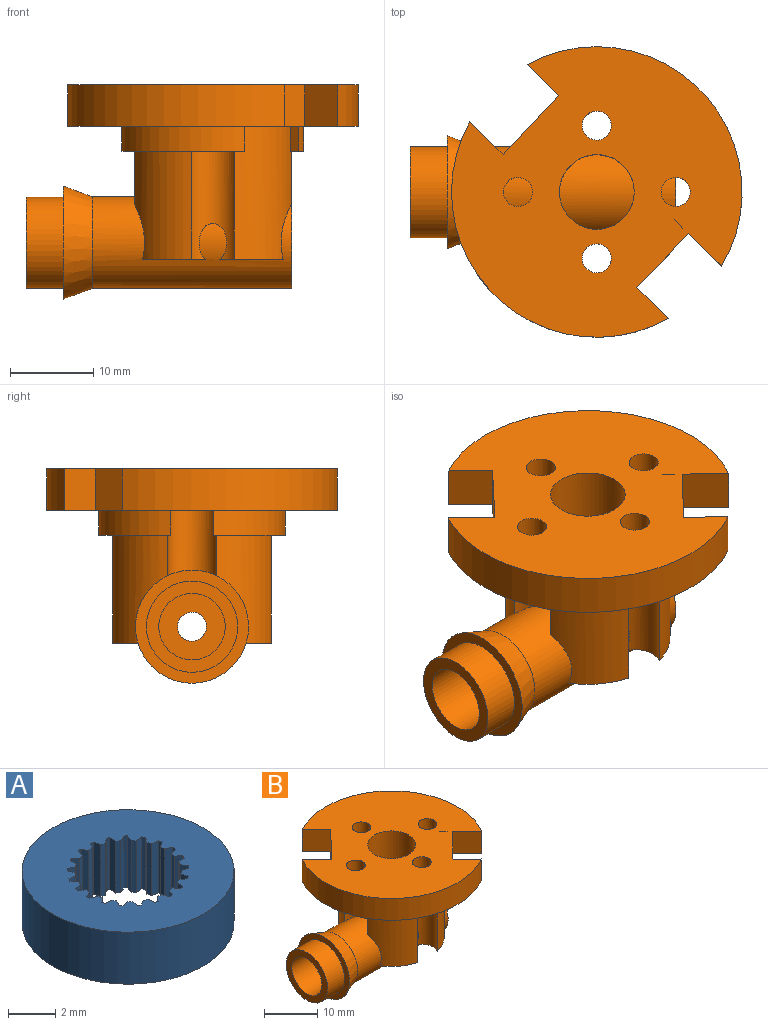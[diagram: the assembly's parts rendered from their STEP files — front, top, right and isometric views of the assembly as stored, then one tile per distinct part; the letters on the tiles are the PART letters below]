
ASSEMBLY  parts=2 mates=1
PART A: 87 faces, bbox 9x9x2.7 mm
  f0: cylinder r=2.58mm len=2.7mm, axis (0,0,-1), area 0.5mm2, adj f22,f24,f25,f57
  f1: cylinder r=2.58mm len=2.7mm, axis (0,0,-1), area 0.5mm2, adj f24,f25,f55,f56
  f2: cylinder r=2.58mm len=2.7mm, axis (0,0,-1), area 0.5mm2, adj f24,f25,f53,f54
  f3: cylinder r=2.58mm len=2.7mm, axis (0,0,-1), area 0.5mm2, adj f24,f25,f51,f52
  f4: cylinder r=2.58mm len=2.7mm, axis (0,0,-1), area 0.5mm2, adj f24,f25,f49,f50
  f5: cylinder r=2.58mm len=2.7mm, axis (0,0,-1), area 0.5mm2, adj f24,f25,f47,f48
  f6: cylinder r=2.58mm len=2.7mm, axis (0,0,-1), area 0.5mm2, adj f24,f25,f45,f46
  f7: cylinder r=2.58mm len=2.7mm, axis (0,0,-1), area 0.5mm2, adj f24,f25,f43,f44
  f8: cylinder r=2.58mm len=2.7mm, axis (0,0,-1), area 0.5mm2, adj f24,f25,f41,f42
  f9: cylinder r=2.58mm len=2.7mm, axis (0,0,-1), area 0.5mm2, adj f24,f25,f39,f40
  f10: cylinder r=2.58mm len=2.7mm, axis (0,0,-1), area 0.5mm2, adj f24,f25,f37,f38
  f11: cylinder r=2.58mm len=2.7mm, axis (0,0,-1), area 0.5mm2, adj f24,f25,f35,f36
  f12: cylinder r=2.58mm len=2.7mm, axis (0,0,-1), area 0.5mm2, adj f24,f25,f33,f34
  f13: cylinder r=2.58mm len=2.7mm, axis (0,0,-1), area 0.5mm2, adj f24,f25,f31,f32
  f14: cylinder r=2.58mm len=2.7mm, axis (0,0,-1), area 0.5mm2, adj f24,f25,f29,f30
  f15: cylinder r=2.58mm len=2.7mm, axis (0,0,-1), area 0.5mm2, adj f24,f25,f27,f28
  f16: cylinder r=2.58mm len=2.7mm, axis (0,0,-1), area 0.5mm2, adj f24,f25,f26,f64
  f17: cylinder r=2.58mm len=2.7mm, axis (0,0,-1), area 0.5mm2, adj f24,f25,f63,f65
  f18: cylinder r=2.58mm len=2.7mm, axis (0,0,-1), area 0.5mm2, adj f24,f25,f61,f62
  f19: cylinder r=2.58mm len=2.7mm, axis (0,0,-1), area 0.5mm2, adj f24,f25,f58,f60
  f20: plane 2.7x0.31mm, normal (0.86,-0.51,0), area 1mm2, adj f21,f24,f25,f86
  f21: cylinder r=2.58mm len=2.7mm, axis (0,0,-1), area 0.5mm2, adj f20,f24,f25,f59
  f22: plane 2.7x0.31mm, normal (-0.86,-0.51,0), area 1mm2, adj f0,f24,f25,f86
  f23: cylinder r=4.5mm len=9mm, axis (0,0,-1), area 76.3mm2, adj f24,f25
  f24: plane 9x9mm, normal (0,0,1), area 45.6mm2, adj f0,f1,f2,f3,f4,f5,f6,f7
  f25: plane 9x9mm, normal (0,0,-1), area 45.6mm2, adj f0,f1,f2,f3,f4,f5,f6,f7
  f26: plane 2.7x0.3mm, normal (-0.58,0.82,0), area 1mm2, adj f16,f24,f25,f85
  f27: plane 2.7x0.32mm, normal (-0.45,-0.89,0), area 1mm2, adj f15,f24,f25,f85
  f28: plane 2.7x0.34mm, normal (-0.31,0.95,0), area 1mm2, adj f15,f24,f25,f84
  f29: plane 2.7x0.26mm, normal (-0.69,-0.72,0), area 1mm2, adj f14,f24,f25,f84
  f30: plane 2.7x0.36mm, normal (-0.02,1,0), area 1mm2, adj f14,f24,f25,f83
  f31: plane 2.7x0.32mm, normal (-0.87,-0.49,0), area 1mm2, adj f13,f24,f25,f83
  f32: plane 2.7x0.35mm, normal (0.28,0.96,0), area 1mm2, adj f13,f24,f25,f82
  f33: plane 2.7x0.35mm, normal (-0.98,-0.21,0), area 1mm2, adj f12,f24,f25,f82
  f34: plane 2.7x0.3mm, normal (0.55,0.84,0), area 1mm2, adj f12,f24,f25,f81
  f35: plane 2.7x0.36mm, normal (-1,0.09,0), area 1mm2, adj f11,f24,f25,f81
  f36: plane 2.7x0.28mm, normal (0.77,0.64,0), area 1mm2, adj f11,f24,f25,f80
  f37: plane 2.7x0.33mm, normal (-0.92,0.38,0), area 1mm2, adj f10,f24,f25,f80
  f38: plane 2.7x0.33mm, normal (0.92,0.38,0), area 1mm2, adj f10,f24,f25,f79
  f39: plane 2.7x0.28mm, normal (-0.77,0.64,0), area 1mm2, adj f9,f24,f25,f79
  f40: plane 2.7x0.36mm, normal (1,0.09,0), area 1mm2, adj f9,f24,f25,f78
  f41: plane 2.7x0.3mm, normal (-0.55,0.84,0), area 1mm2, adj f8,f24,f25,f78
  f42: plane 2.7x0.35mm, normal (0.98,-0.21,0), area 1mm2, adj f8,f24,f25,f77
  f43: plane 2.7x0.35mm, normal (-0.28,0.96,0), area 1mm2, adj f7,f24,f25,f77
  f44: plane 2.7x0.32mm, normal (0.87,-0.49,0), area 1mm2, adj f7,f24,f25,f76
  f45: plane 2.7x0.36mm, normal (0.02,1,0), area 1mm2, adj f6,f24,f25,f76
  f46: plane 2.7x0.26mm, normal (0.69,-0.72,0), area 1mm2, adj f6,f24,f25,f75
  f47: plane 2.7x0.34mm, normal (0.31,0.95,0), area 1mm2, adj f5,f24,f25,f75
  f48: plane 2.7x0.32mm, normal (0.45,-0.89,0), area 1mm2, adj f5,f24,f25,f74
  f49: plane 2.7x0.3mm, normal (0.58,0.82,0), area 1mm2, adj f4,f24,f25,f74
  f50: plane 2.7x0.36mm, normal (0.17,-0.99,0), area 1mm2, adj f4,f24,f25,f73
  f51: plane 2.7x0.29mm, normal (0.79,0.61,0), area 1mm2, adj f3,f24,f25,f73
  f52: plane 2.7x0.36mm, normal (-0.13,-0.99,0), area 1mm2, adj f3,f24,f25,f72
  f53: plane 2.7x0.34mm, normal (0.94,0.35,0), area 1mm2, adj f2,f24,f25,f72
  f54: plane 2.7x0.33mm, normal (-0.42,-0.91,0), area 1mm2, adj f2,f24,f25,f71
  f55: plane 2.7x0.36mm, normal (1,0.06,0), area 1mm2, adj f1,f24,f25,f71
  f56: plane 2.7x0.27mm, normal (-0.67,-0.74,0), area 1mm2, adj f1,f24,f25,f70
  f57: plane 2.7x0.35mm, normal (0.97,-0.24,0), area 1mm2, adj f0,f24,f25,f70
  f58: plane 2.7x0.27mm, normal (0.67,-0.74,0), area 1mm2, adj f19,f24,f25,f69
  f59: plane 2.7x0.35mm, normal (-0.97,-0.24,0), area 1mm2, adj f21,f24,f25,f69
  f60: plane 2.7x0.36mm, normal (-1,0.06,0), area 1mm2, adj f19,f24,f25,f68
  f61: plane 2.7x0.33mm, normal (0.42,-0.91,0), area 1mm2, adj f18,f24,f25,f68
  f62: plane 2.7x0.34mm, normal (-0.94,0.35,0), area 1mm2, adj f18,f24,f25,f67
  f63: plane 2.7x0.36mm, normal (0.13,-0.99,0), area 1mm2, adj f17,f24,f25,f67
  f64: plane 2.7x0.36mm, normal (-0.17,-0.99,0), area 1mm2, adj f16,f24,f25,f66
  f65: plane 2.7x0.29mm, normal (-0.79,0.61,0), area 1mm2, adj f17,f24,f25,f66
  f66: cylinder r=2.25mm len=2.7mm, axis (0,0,1), area 0.6mm2, adj f24,f25,f64,f65
  f67: cylinder r=2.25mm len=2.7mm, axis (0,0,1), area 0.6mm2, adj f24,f25,f62,f63
  f68: cylinder r=2.25mm len=2.7mm, axis (0,0,1), area 0.6mm2, adj f24,f25,f60,f61
  f69: cylinder r=2.25mm len=2.7mm, axis (0,0,1), area 0.6mm2, adj f24,f25,f58,f59
  f70: cylinder r=2.25mm len=2.7mm, axis (0,0,1), area 0.6mm2, adj f24,f25,f56,f57
  f71: cylinder r=2.25mm len=2.7mm, axis (0,0,1), area 0.6mm2, adj f24,f25,f54,f55
  f72: cylinder r=2.25mm len=2.7mm, axis (0,0,1), area 0.6mm2, adj f24,f25,f52,f53
  f73: cylinder r=2.25mm len=2.7mm, axis (0,0,1), area 0.6mm2, adj f24,f25,f50,f51
  f74: cylinder r=2.25mm len=2.7mm, axis (0,0,1), area 0.6mm2, adj f24,f25,f48,f49
  f75: cylinder r=2.25mm len=2.7mm, axis (0,0,1), area 0.6mm2, adj f24,f25,f46,f47
  f76: cylinder r=2.25mm len=2.7mm, axis (0,0,1), area 0.6mm2, adj f24,f25,f44,f45
  f77: cylinder r=2.25mm len=2.7mm, axis (0,0,1), area 0.6mm2, adj f24,f25,f42,f43
  f78: cylinder r=2.25mm len=2.7mm, axis (0,0,1), area 0.6mm2, adj f24,f25,f40,f41
  f79: cylinder r=2.25mm len=2.7mm, axis (0,0,1), area 0.6mm2, adj f24,f25,f38,f39
  f80: cylinder r=2.25mm len=2.7mm, axis (0,0,1), area 0.6mm2, adj f24,f25,f36,f37
  f81: cylinder r=2.25mm len=2.7mm, axis (0,0,1), area 0.6mm2, adj f24,f25,f34,f35
  f82: cylinder r=2.25mm len=2.7mm, axis (0,0,1), area 0.6mm2, adj f24,f25,f32,f33
  f83: cylinder r=2.25mm len=2.7mm, axis (0,0,1), area 0.6mm2, adj f24,f25,f30,f31
  f84: cylinder r=2.25mm len=2.7mm, axis (0,0,1), area 0.6mm2, adj f24,f25,f28,f29
  f85: cylinder r=2.25mm len=2.7mm, axis (0,0,1), area 0.6mm2, adj f24,f25,f26,f27
  f86: cylinder r=2.25mm len=2.7mm, axis (0,0,1), area 0.6mm2, adj f20,f22,f24,f25
PART B: 52 faces, bbox 40x35x25.8 mm
  f0: plane 11x11mm, normal (-1,0,0), area 44.8mm2, adj f47,f49
  f1: cylinder r=5.5mm len=24mm, axis (-1,0,0), area 497.6mm2, adj f2,f4,f5,f6,f7,f8,f9,f10
  f2: cylinder r=5.5mm len=3.32mm, axis (-1,0,0), area 6.2mm2, adj f1,f9
  f3: cylinder r=4.5mm len=15.84mm, axis (0,0,-1), area 412.5mm2, adj f34,f42
  f4: cylinder r=9.9mm len=13mm, axis (0,0,1), area 114.7mm2, adj f1,f5,f11,f15,f39
  f5: cylinder r=3mm len=16mm, axis (0,0,1), area 209.5mm2, adj f1,f4,f6,f14,f15,f16,f39
  f6: cylinder r=9.9mm len=16mm, axis (0,0,1), area 142.8mm2, adj f1,f5,f7,f14,f17,f26,f38,f39
  f7: cylinder r=3mm len=9.39mm, axis (0,0,1), area 92.4mm2, adj f1,f6,f8,f17,f35,f36,f40,f41
  f8: cylinder r=9.9mm len=13mm, axis (0,0,1), area 114.7mm2, adj f1,f7,f9,f13,f36
  f9: cylinder r=3mm len=16mm, axis (0,0,1), area 209.5mm2, adj f1,f2,f8,f10,f12,f13,f18,f36
  f10: cylinder r=9.9mm len=13mm, axis (0,0,1), area 114.7mm2, adj f1,f9,f11,f12,f36
  f11: cylinder r=3mm len=9.39mm, axis (0,0,1), area 92.4mm2, adj f1,f4,f10,f17,f35,f36,f37,f39
  f12: plane 7.62x4.44mm, normal (0,0,-1), area 16.6mm2, adj f1,f9,f10
  f13: plane 7.62x4.44mm, normal (0,0,-1), area 16.6mm2, adj f1,f8,f9
  f14: plane 7.62x4.44mm, normal (0,0,-1), area 16.6mm2, adj f1,f5,f6
  f15: plane 7.62x4.44mm, normal (0,0,-1), area 16.6mm2, adj f1,f4,f5
  f16: plane 6x6mm, normal (0,0,-1), area 18.7mm2, adj f5,f31
  f17: plane 35x35mm, normal (0,0,-1), area 494.1mm2, adj f6,f7,f11,f19,f20,f21,f22,f23
  f18: plane 6x6mm, normal (0,0,-1), area 18.7mm2, adj f9,f29
  f19: plane 6.48x6.25mm, normal (0.72,-0.69,0), area 45mm2, adj f17,f20,f28,f34
  f20: plane 5x4mm, normal (-0.7,-0.72,0), area 27.9mm2, adj f17,f19,f21,f34
  f21: cylinder r=17.5mm len=26.41mm, axis (0,0,-1), area 228mm2, adj f17,f20,f22,f34
  f22: plane 5x3.83mm, normal (-0.69,-0.72,0), area 26.6mm2, adj f17,f21,f23,f34
  f23: plane 7.13x6.71mm, normal (-0.73,0.69,0), area 49mm2, adj f17,f22,f24,f34
  f24: plane 5x4.04mm, normal (0.69,0.72,0), area 28.1mm2, adj f17,f23,f25,f34
  f25: cylinder r=17.5mm len=26.16mm, axis (0,0,-1), area 226.7mm2, adj f17,f24,f28,f34
  f26: plane 8x1.05mm, normal (-0.69,-0.72,0), area 11.7mm2, adj f6,f27,f30,f34,f40,f41
  f27: cylinder r=11.25mm len=5mm, axis (0,0,-1), area 0mm2, adj f17,f26,f30,f34
  f28: plane 5x3.85mm, normal (0.69,0.72,0), area 26.7mm2, adj f17,f19,f25,f34
  f29: cylinder r=1.75mm len=5mm, axis (0,0,-1), area 55mm2, adj f18,f34
  f30: plane 5x1.05mm, normal (0.7,0.72,0), area 7.3mm2, adj f17,f26,f27,f34
  f31: cylinder r=1.75mm len=5mm, axis (0,0,-1), area 55mm2, adj f16,f34
  f32: cylinder r=1.75mm len=5mm, axis (0,0,-1), area 55mm2, adj f17,f34
  f33: cylinder r=1.75mm len=5mm, axis (0,0,-1), area 55mm2, adj f17,f34
  f34: plane 35x35mm, normal (0,0,1), area 749.2mm2, adj f3,f19,f20,f21,f22,f23,f24,f25
  f35: cylinder r=11.25mm len=21.88mm, axis (0,0,1), area 90.1mm2, adj f7,f11,f17,f36
  f36: plane 21.88x8.62mm, normal (0,0,-1), area 32.9mm2, adj f7,f8,f9,f10,f11,f35
  f37: cylinder r=11.25mm len=14.79mm, axis (0,0,1), area 56.8mm2, adj f11,f17,f38,f39
  f38: plane 3x1.1mm, normal (0.69,0.72,0), area 4.6mm2, adj f6,f17,f37,f39
  f39: plane 14.79x8.62mm, normal (0,0,-1), area 19mm2, adj f4,f5,f6,f11,f37,f38
  f40: cylinder r=11.25mm len=3mm, axis (0,0,1), area 5.4mm2, adj f7,f17,f26,f41
  f41: plane 1.71x1.61mm, normal (0,0,-1), area 1.3mm2, adj f6,f7,f26,f40
  f42: cylinder r=5.5mm len=9mm, axis (-1,0,0), area 71.1mm2, adj f3
  f43: plane 11x11mm, normal (1,0,0), area 31.4mm2, adj f1,f44
  f44: cylinder r=4.5mm len=9mm, axis (1,0,0), area 84.8mm2, adj f43,f45
  f45: plane 9x9mm, normal (1,0,0), area 54mm2, adj f44,f46
  f46: cylinder r=1.75mm len=4mm, axis (-1,0,0), area 44mm2, adj f45,f48
  f47: cylinder r=4mm len=25mm, axis (-1,0,0), area 628.3mm2, adj f0,f48
  f48: plane 8x8mm, normal (-1,0,0), area 40.6mm2, adj f46,f47
  f49: cylinder r=5.5mm len=11mm, axis (-1,0,0), area 155.5mm2, adj f0,f50
  f50: plane 13.63x13.63mm, normal (-1,0,0), area 50.8mm2, adj f49,f51
  f51: cone r=7mm half-angle=20.6deg, axis (-1,0,0), area 144.6mm2, adj f1,f50
PLACE A rot(axis=(0,1,0),90deg) t=(-2.65,-3.58,-12.8)mm
PLACE B t=(-9.15,-3.58,1.2)mm
MATE fastened A.f0 <-> B.f1  axis (-1,0,0) through (-2.65,-3.58,-12.8)mm
